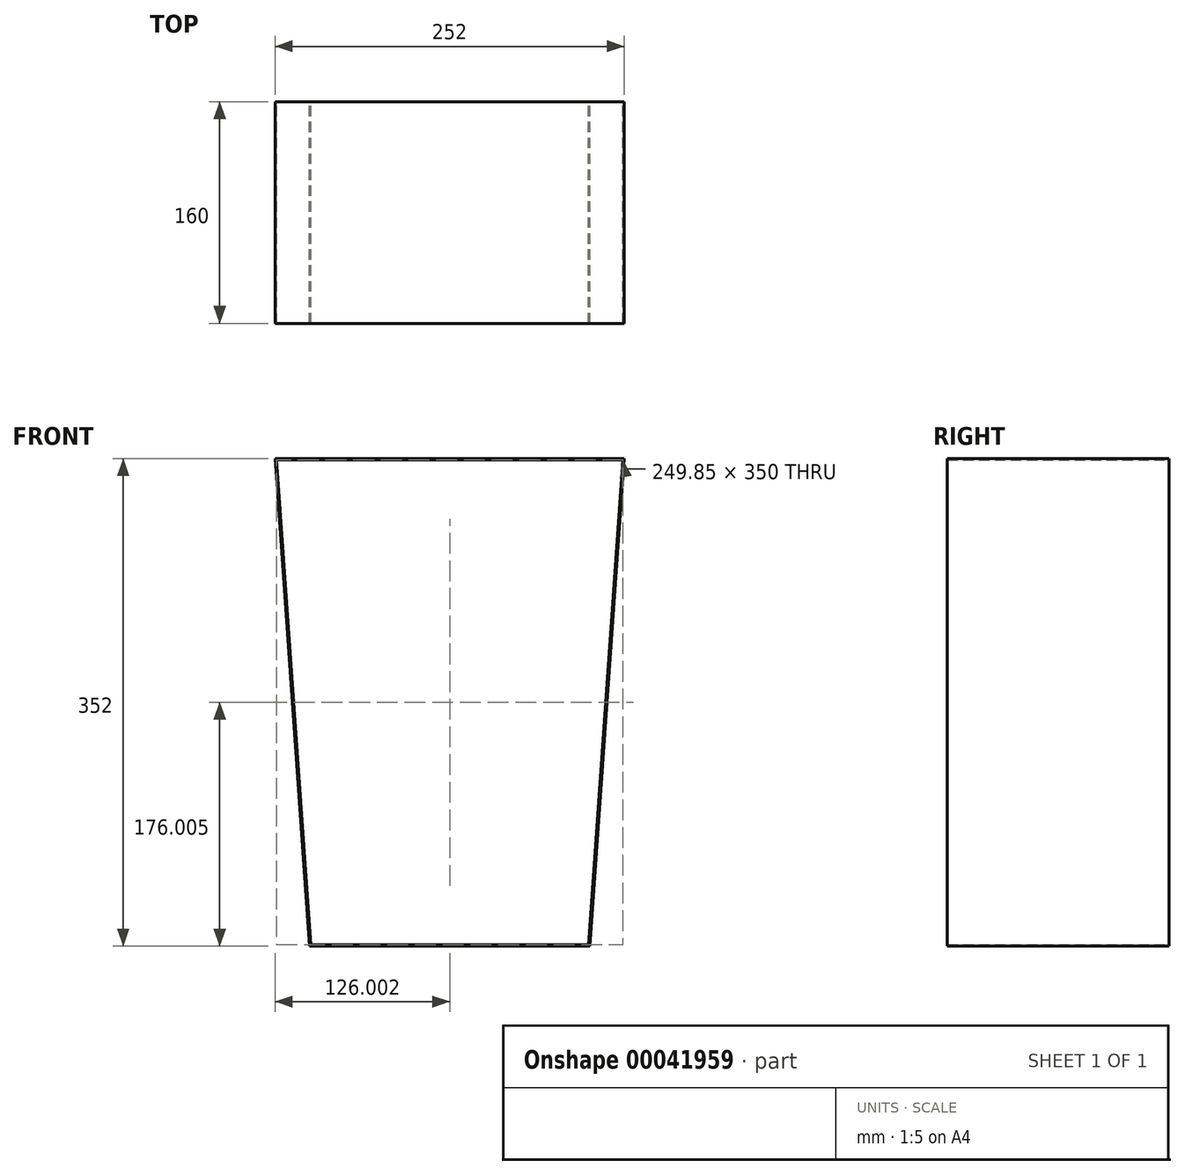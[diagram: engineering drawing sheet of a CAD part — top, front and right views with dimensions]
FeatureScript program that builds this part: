
annotation { "Feature Type Name" : "Feature", "Feature Type Description" : "" }
export const myFeature = defineFeature(function(context is Context, id is Id, definition is map)
    precondition{}
    {
        {
            var Q0;
            Q0=qCreatedBy(makeId("Front.planeOp"),FACE);
            var sketch = newSketch(context, id + "F0", { "sketchPlane" : qUnion([Q0])});
            skLineSegment(sketch, "E0", {"start": v(-1.1, 210.15) * mm, "end": v(-1.1, -219.8) * mm});
            skLineSegment(sketch, "E1", {"start": v(-127.1, 121.17) * mm, "end": v(124.9, 121.17) * mm});
            skLineSegment(sketch, "E2", {"start": v(-102.1, -230.83) * mm, "end": v(99.9, -230.83) * mm});
            skLineSegment(sketch, "E3", {"start": v(-127.1, 121.17) * mm, "end": v(-102.1, -230.83) * mm});
            skLineSegment(sketch, "E4", {"start": v(124.9, 121.17) * mm, "end": v(99.9, -230.83) * mm});
            skLineSegment(sketch, "E5.0", {"start": v(-126.03, 120.17) * mm, "end": v(123.82, 120.17) * mm});
            skLineSegment(sketch, "E5.1", {"start": v(-126.03, 120.17) * mm, "end": v(-101.18, -229.83) * mm});
            skLineSegment(sketch, "E5.2", {"start": v(-101.18, -229.83) * mm, "end": v(98.96, -229.83) * mm});
            skLineSegment(sketch, "E5.3", {"start": v(123.82, 120.17) * mm, "end": v(98.96, -229.83) * mm});
            skSolve(sketch);
        }
        {
            var Q0;
            Q0=makeQuery(id+"F0.imprint","IMPRINT",FACE,{"disambiguationData":[TD([[makeQuery(id+"F0.imprint","IMPRINT",EDGE,{"derivedFrom":sQuery(id+"F0.wireOp",EDGE,"E2")}),1.0]])]});
            extrude(context, id + "F1", {"entities" : qUnion([Q0]), "depth" : 160 * mm});
        }
    });
